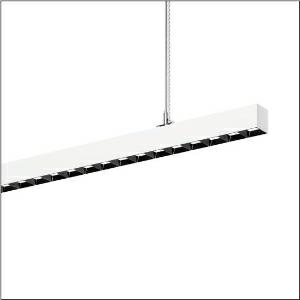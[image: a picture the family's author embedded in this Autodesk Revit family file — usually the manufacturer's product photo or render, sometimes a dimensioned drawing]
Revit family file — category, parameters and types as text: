
# Revit family: silica_r__21_51mx32dc4dwb_0a61
name_source: partatom
category: Lighting Fixtures
units: mm (PartAtom-declared; Revit-internal decimal feet)

## family parameters
Cut with Voids When Loaded = No
Host = Face
Light Source = No
Part Type = Normal
Room Calculation Point = No
Round Connector Dimension = Use Diameter
Shared = No

## types (1)
- --- (1 x LED, 18230 lm, 105.8 W, 4000K)
    Apparent Load = 106 VA
    CIE Flux Codes = 86 99 100 59 100
    Color Rendering = 80
    Color Temperature = 4000K
    Default Elevation = 1800 mm
    Description = Silica® 21, office luminaire, primary light control with darklight reflector, of PMMA, black, CAT 2 (L<= 3000cd/m²), light emission: direct/indirect distribution, primary light characteristic: symmetric, installation type: suspended mounting, LED, rated luminous flux: 18.230lm, luminous efficacy: 172lm/W, light colour: 840, colour temperature: 4000K, with terminal, 3+2-pole, max. 2.5mm², mains connection: 220..240V, AC, 50/60Hz, rated input power: 105.8W, luminaire housing, of aluminium, traffic white (RAL 9016), length: 3.004mm, width: 53mm, height: 53mm, protection rating (complete): IP20, insulation class (complete): insulation class I (protective earthing), certification: CE, permissible operating ambient temperature: 0..+35°C, standard: EN 50419, packaging unit: 1 piece
    Height = 53 mm
    Lamp = 1 x LED
    Lamp Light Flux = 18230 lm
    Lamp Power = 105.8 W
    Lamp count = 1
    Length = 3004 mm
    Luminous efficacy = 172 lm/W
    Manufacturer = Siteco
    ModVariant = No
    Model = 51MX32DC4DWB
    Mounting Place = Ceiling
    Mounting Type = Pendant
    Number of Poles = 1
    OnlyDefault = Yes
    Power Factor = 1
    Product Name = Silica® 21
    Product group = office luminaire | ceiling pendant
    ProductGroupID = 905
    Protection Class = Protection class I
    Protection Degree = IP 20
    RLX_Detail_Level = 1
    RlxData = <blob elided: 64345 chars, md5=c7030718>
    Socket = socket
    Standby Power = 0 W
    System Light Flux = 18230 lm
    System Power = 106 W
    Type Comments = factory setting: luminous flux: 100 % | dim-lin: 254 | 366 mA
    Type Image = l_1251637.jpg
    URL = http://relux.com
    VarID = @adj_031421
    Voltage = 0 V
    Weight = 0.00 kg
    Width = 53 mm

## geometry (parser evidence)
native form markers: Blend x4, Sweep x13
no freeform markers — native parametric forms only
